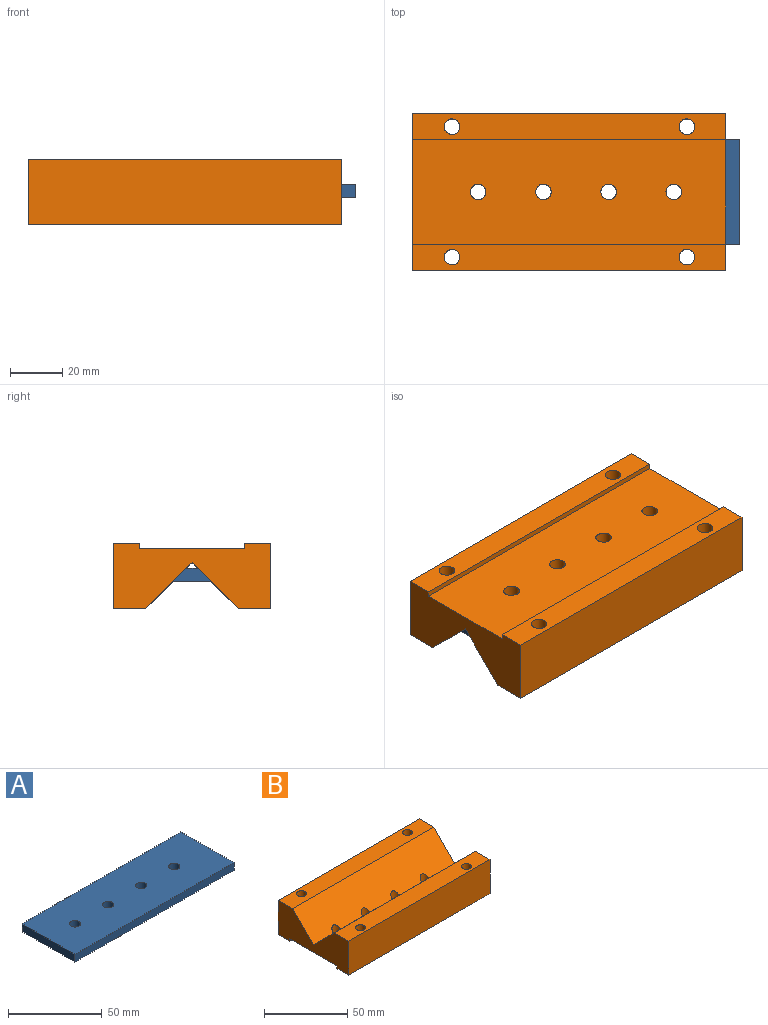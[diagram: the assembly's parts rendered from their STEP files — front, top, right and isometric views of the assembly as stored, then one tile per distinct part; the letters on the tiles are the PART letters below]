
ASSEMBLY  parts=2 mates=1
PART A: 10 faces, bbox 120x40x5 mm
  f0: plane 120x5mm, normal (0,1,0), area 600mm2, adj f1,f7,f8,f9
  f1: plane 40x5mm, normal (-1,0,0), area 200mm2, adj f0,f2,f8,f9
  f2: plane 120x5mm, normal (0,-1,0), area 600mm2, adj f1,f7,f8,f9
  f3: cylinder r=3mm len=6mm, axis (0,0,-1), area 94.2mm2, adj f8,f9
  f4: cylinder r=3mm len=6mm, axis (0,0,-1), area 94.2mm2, adj f8,f9
  f5: cylinder r=3mm len=6mm, axis (0,0,-1), area 94.2mm2, adj f8,f9
  f6: cylinder r=3mm len=6mm, axis (0,0,-1), area 94.2mm2, adj f8,f9
  f7: plane 40x5mm, normal (1,0,0), area 200mm2, adj f0,f2,f8,f9
  f8: plane 120x40mm, normal (0,0,1), area 4686.9mm2, adj f0,f1,f2,f3,f4,f5,f6,f7
  f9: plane 120x40mm, normal (0,0,-1), area 4686.9mm2, adj f0,f1,f2,f3,f4,f5,f6,f7
PART B: 21 faces, bbox 120x60x25 mm
  f0: plane 120x12.32mm, normal (0,0,1), area 1422.1mm2, adj f4,f5,f10,f15,f19,f20
  f1: plane 120x10mm, normal (0,0,-1), area 1143.5mm2, adj f4,f5,f10,f12,f19,f20
  f2: plane 120x10mm, normal (0,0,-1), area 1143.5mm2, adj f4,f5,f11,f13,f17,f18
  f3: plane 120x12.32mm, normal (0,0,1), area 1422.1mm2, adj f4,f5,f11,f16,f17,f18
  f4: plane 60x25mm, normal (1,0,0), area 1107.5mm2, adj f0,f1,f2,f3,f10,f11,f12,f13
  f5: plane 60x25mm, normal (-1,0,0), area 1107.5mm2, adj f0,f1,f2,f3,f10,f11,f12,f13
  f6: cylinder r=3mm len=8.33mm, axis (0,0,-1), area 136.3mm2, adj f14,f15,f16
  f7: cylinder r=3mm len=8.33mm, axis (0,0,-1), area 136.3mm2, adj f14,f15,f16
  f8: cylinder r=3mm len=8.33mm, axis (0,0,-1), area 136.3mm2, adj f14,f15,f16
  f9: cylinder r=3mm len=8.33mm, axis (0,0,-1), area 136.3mm2, adj f14,f15,f16
  f10: plane 120x25mm, normal (0,1,0), area 3000mm2, adj f0,f1,f4,f5
  f11: plane 120x25mm, normal (0,-1,0), area 3000mm2, adj f2,f3,f4,f5
  f12: plane 120x2mm, normal (0,-1,0), area 240mm2, adj f1,f4,f5,f14
  f13: plane 120x2mm, normal (0,1,0), area 240mm2, adj f2,f4,f5,f14
  f14: plane 120x40mm, normal (0,0,-1), area 4686.9mm2, adj f4,f5,f6,f7,f8,f9,f12,f13
  f15: plane 120x17.68mm, normal (0,-0.71,0.71), area 2920mm2, adj f0,f4,f5,f6,f7,f8,f9,f16
  f16: plane 120x17.68mm, normal (0,0.71,0.71), area 2920mm2, adj f3,f4,f5,f6,f7,f8,f9,f15
  f17: cylinder r=3mm len=25mm, axis (0,0,-1), area 471.2mm2, adj f2,f3
  f18: cylinder r=3mm len=25mm, axis (0,0,-1), area 471.2mm2, adj f2,f3
  f19: cylinder r=3mm len=25mm, axis (0,0,-1), area 471.2mm2, adj f0,f1
  f20: cylinder r=3mm len=25mm, axis (0,0,-1), area 471.2mm2, adj f0,f1
PLACE A t=(-70.8,-27.95,31.78)mm
PLACE B rot(axis=(0,1,0),180deg) t=(-50.66,-16.64,46.32)mm
MATE cylindrical B.f8 <-> A.f3  axis (0,0,1) through (-102.07,-7.95,44.32)mm
